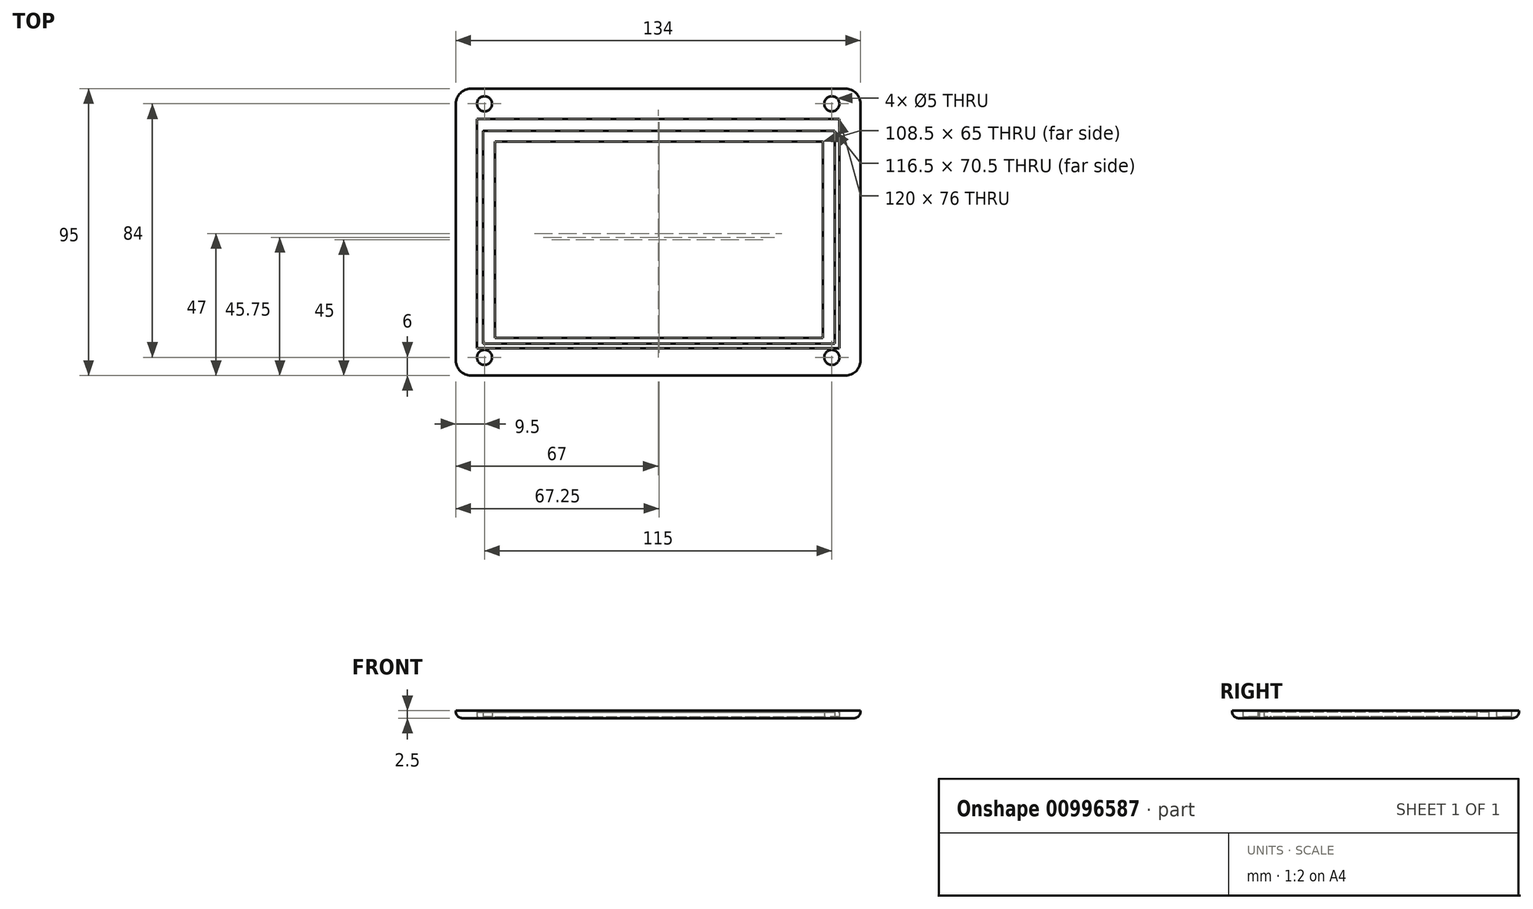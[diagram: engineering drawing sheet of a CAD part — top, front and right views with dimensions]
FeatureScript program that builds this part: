
annotation { "Feature Type Name" : "Feature", "Feature Type Description" : "" }
export const myFeature = defineFeature(function(context is Context, id is Id, definition is map)
    precondition{}
    {
        {
            var Q0;
            Q0=qCreatedBy(makeId("Top.planeOp"),FACE);
            var sketch = newSketch(context, id + "F0", { "sketchPlane" : qUnion([Q0])});
            skLineSegment(sketch, "E0.bottom", {"start": v(-62, 47.5) * mm, "end": v(62, 47.5) * mm});
            skLineSegment(sketch, "E0.top", {"start": v(-62, -47.5) * mm, "end": v(62, -47.5) * mm});
            skLineSegment(sketch, "E0.left", {"start": v(-67, 42.5) * mm, "end": v(-67, -42.5) * mm});
            skLineSegment(sketch, "E0.right", {"start": v(67, 42.5) * mm, "end": v(67, -42.5) * mm});
            skPoint(sketch, "E0.middle", {"position": v(0, 0) * mm});
            skLineSegment(sketch, "E1.bottom", {"start": v(-60, 37.5) * mm, "end": v(60, 37.5) * mm});
            skLineSegment(sketch, "E1.top", {"start": v(-60, -38.5) * mm, "end": v(60, -38.5) * mm});
            skLineSegment(sketch, "E1.left", {"start": v(-60, 37.5) * mm, "end": v(-60, -38.5) * mm});
            skLineSegment(sketch, "E1.right", {"start": v(60, 37.5) * mm, "end": v(60, -38.5) * mm});
            skPoint(sketch, "E2.visualSharp", {"position": v(-67, 47.5) * mm});
            skArc(sketch, "E2.filletArc", {"start": v(-62, 47.5) * mm, "mid": v(-65.54, 46.04) * mm, "end": v(-67, 42.5) * mm});
            skPoint(sketch, "E3.visualSharp", {"position": v(67, 47.5) * mm});
            skArc(sketch, "E3.filletArc", {"start": v(67, 42.5) * mm, "mid": v(65.54, 46.04) * mm, "end": v(62, 47.5) * mm});
            skPoint(sketch, "E4.visualSharp", {"position": v(67, -47.5) * mm});
            skArc(sketch, "E4.filletArc", {"start": v(62, -47.5) * mm, "mid": v(65.54, -46.04) * mm, "end": v(67, -42.5) * mm});
            skPoint(sketch, "E5.visualSharp", {"position": v(-67, -47.5) * mm});
            skArc(sketch, "E5.filletArc", {"start": v(-67, -42.5) * mm, "mid": v(-65.54, -46.04) * mm, "end": v(-62, -47.5) * mm});
            skLineSegment(sketch, "E6.bottom", {"start": v(-58, 33.5) * mm, "end": v(58.5, 33.5) * mm});
            skLineSegment(sketch, "E6.top", {"start": v(-58, -37) * mm, "end": v(58.5, -37) * mm});
            skLineSegment(sketch, "E6.left", {"start": v(-58, 33.5) * mm, "end": v(-58, -37) * mm});
            skLineSegment(sketch, "E6.right", {"start": v(58.5, 33.5) * mm, "end": v(58.5, -37) * mm});
            skLineSegment(sketch, "E7.bottom", {"start": v(-54, 30) * mm, "end": v(54.5, 30) * mm});
            skLineSegment(sketch, "E7.top", {"start": v(-54, -35) * mm, "end": v(54.5, -35) * mm});
            skLineSegment(sketch, "E7.left", {"start": v(-54, 30) * mm, "end": v(-54, -35) * mm});
            skLineSegment(sketch, "E7.right", {"start": v(54.5, 30) * mm, "end": v(54.5, -35) * mm});
            skCircle(sketch, "E8", {"center": v(57.5, -41.5) * mm, "radius": 2.5 * mm});
            skCircle(sketch, "E9", {"center": v(57.5, 42.5) * mm, "radius": 2.5 * mm});
            skCircle(sketch, "E10", {"center": v(-57.5, 42.5) * mm, "radius": 2.5 * mm});
            skCircle(sketch, "E11", {"center": v(-57.5, -41.5) * mm, "radius": 2.5 * mm});
            skSolve(sketch);
        }
        {
            var Q0;
            Q0=makeQuery(id+"F0.imprint","IMPRINT",FACE,{"disambiguationData":[TD([[makeQuery(id+"F0.imprint","IMPRINT",EDGE,{"derivedFrom":sQuery(id+"F0.wireOp",EDGE,"E0.bottom")}),-1.0]])]});
            extrude(context, id + "F1", {"entities" : qUnion([Q0]), "depth" : 2.5 * mm, "offsetDistance" : 25.4 * mm});
        }
        {
            var Q0;
            Q0=makeQuery(id+"F0.imprint","IMPRINT",FACE,{"disambiguationData":[TD([[makeQuery(id+"F0.imprint","IMPRINT",EDGE,{"derivedFrom":sQuery(id+"F0.wireOp",EDGE,"E6.bottom")}),-1.0]])]});
            var Q1;
            Q1=makeQuery(id+"F0.imprint","IMPRINT",FACE,{"disambiguationData":[TD([[makeQuery(id+"F0.imprint","IMPRINT",EDGE,{"derivedFrom":sQuery(id+"F0.wireOp",EDGE,"E9")}),1.0]])]});
            var Q2;
            Q2=makeQuery(id+"F0.imprint","IMPRINT",FACE,{"disambiguationData":[TD([[makeQuery(id+"F0.imprint","IMPRINT",EDGE,{"derivedFrom":sQuery(id+"F0.wireOp",EDGE,"E8")}),1.0]])]});
            var Q3;
            Q3=makeQuery(id+"F0.imprint","IMPRINT",FACE,{"disambiguationData":[TD([[makeQuery(id+"F0.imprint","IMPRINT",EDGE,{"derivedFrom":sQuery(id+"F0.wireOp",EDGE,"E11")}),1.0]])]});
            var Q4;
            Q4=makeQuery(id+"F0.imprint","IMPRINT",FACE,{"disambiguationData":[TD([[makeQuery(id+"F0.imprint","IMPRINT",EDGE,{"derivedFrom":sQuery(id+"F0.wireOp",EDGE,"E10")}),1.0]])]});
            extrude(context, id + "F2", {"entities" : qUnion([Q0, Q1, Q2, Q3, Q4]), "depth" : 0.5 * mm, "offsetDistance" : 25.4 * mm});
        }
        {
            var Q0;
            Q0=makeQuery(id+"F0.imprint","IMPRINT",FACE,{"disambiguationData":[TD([[makeQuery(id+"F0.imprint","IMPRINT",EDGE,{"derivedFrom":sQuery(id+"F0.wireOp",EDGE,"E1.bottom")}),-1.0]])]});
            extrude(context, id + "F3", {"entities" : qUnion([Q0]), "depth" : 2 * mm, "offsetDistance" : 25.4 * mm});
        }
        {
            var Q0;
            Q0=makeQuery(id+"F1.opExtrude","CAP_EDGE",EDGE,{"disambiguationData":[OSD([sQuery(id+"F0.wireOp",EDGE,"E2.filletArc")])],"isStart":true});
            fillet(context, id + "F4", {"entities" : qUnion([Q0]), "radius" : 2.2 * mm, "tangentPropagation" : true, "allowEdgeOverflow" : false});
        }
    });
